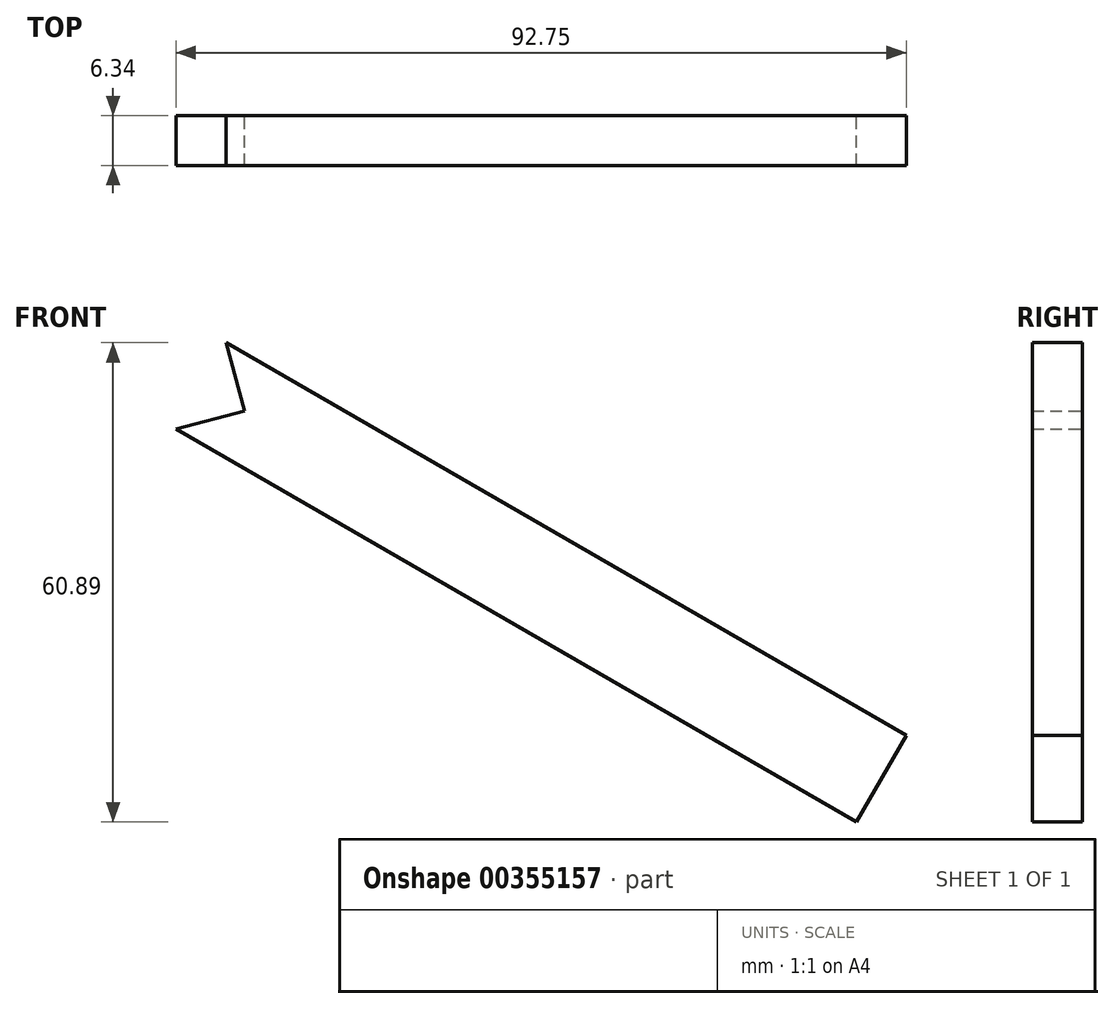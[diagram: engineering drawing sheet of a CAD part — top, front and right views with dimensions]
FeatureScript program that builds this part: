
annotation { "Feature Type Name" : "Feature", "Feature Type Description" : "" }
export const myFeature = defineFeature(function(context is Context, id is Id, definition is map)
    precondition{}
    {
        {
            var Q0;
            Q0=qCreatedBy(makeId("Front.planeOp"),FACE);
            var sketch = newSketch(context, id + "F0", { "sketchPlane" : qUnion([Q0])});
            skLineSegment(sketch, "E0", {"start": v(-87.99, -152.4) * mm, "end": v(263.96, -152.4) * mm, "construction": true});
            skLineSegment(sketch, "E1", {"start": v(263.96, -152.4) * mm, "end": v(0, 0) * mm});
            skLineSegment(sketch, "E2", {"start": v(0, 0) * mm, "end": v(-87.99, -152.4) * mm, "construction": true});
            skLineSegment(sketch, "E3", {"start": v(0, 0) * mm, "end": v(-152.4, 87.99) * mm});
            skCircle(sketch, "E4", {"center": v(0, 0) * mm, "radius": 12.7 * mm});
            skCircle(sketch, "E5", {"center": v(0, 0) * mm, "radius": 9.53 * mm});
            skLineSegment(sketch, "E6", {"start": v(0, 0) * mm, "end": v(6.35, 11) * mm, "construction": true});
            skLineSegment(sketch, "E7", {"start": v(-152.4, 87.99) * mm, "end": v(-146.05, 98.99) * mm});
            skLineSegment(sketch, "E8", {"start": v(-146.05, 98.99) * mm, "end": v(6.35, 11) * mm});
            skLineSegment(sketch, "E9", {"start": v(6.35, 11) * mm, "end": v(270.31, -141.4) * mm});
            skLineSegment(sketch, "E10", {"start": v(270.31, -141.4) * mm, "end": v(263.96, -152.4) * mm});
            skLineSegment(sketch, "E11", {"start": v(-149.23, 93.49) * mm, "end": v(267.14, -146.9) * mm});
            skLineSegment(sketch, "E12", {"start": v(18.93, 3.74) * mm, "end": v(21.25, -4.94) * mm});
            skLineSegment(sketch, "E13", {"start": v(21.25, -4.94) * mm, "end": v(12.58, -7.26) * mm});
            skLineSegment(sketch, "E14", {"start": v(12.58, -7.26) * mm, "end": v(18.93, 3.74) * mm});
            skLineSegment(sketch, "E15", {"start": v(183.9, -91.51) * mm, "end": v(186.23, -100.19) * mm});
            skLineSegment(sketch, "E16", {"start": v(186.23, -100.19) * mm, "end": v(177.56, -102.51) * mm});
            skLineSegment(sketch, "E17", {"start": v(183.9, -91.51) * mm, "end": v(177.56, -102.51) * mm});
            skSolve(sketch);
        }
        {
            var Q0;
            {var subQ3=sQuery(id+"F0.wireOp",EDGE,"E15");Q0=makeQuery(id+"F0.imprint","IMPRINT",FACE,{"disambiguationData":[TD([[makeQuery(id+"F0.imprint","IMPRINT",EDGE,{"derivedFrom":subQ3}),1.0]])]});}
            var Q1;
            {var subQ3=sQuery(id+"F0.wireOp",EDGE,"E16");Q1=makeQuery(id+"F0.imprint","IMPRINT",FACE,{"disambiguationData":[TD([[makeQuery(id+"F0.imprint","IMPRINT",EDGE,{"derivedFrom":subQ3}),1.0]])]});}
            extrude(context, id + "F1", {"entities" : qUnion([Q0, Q1]), "endBound" : BoundingType.SYMMETRIC, "depth" : 6.35 * mm});
        }
    });
